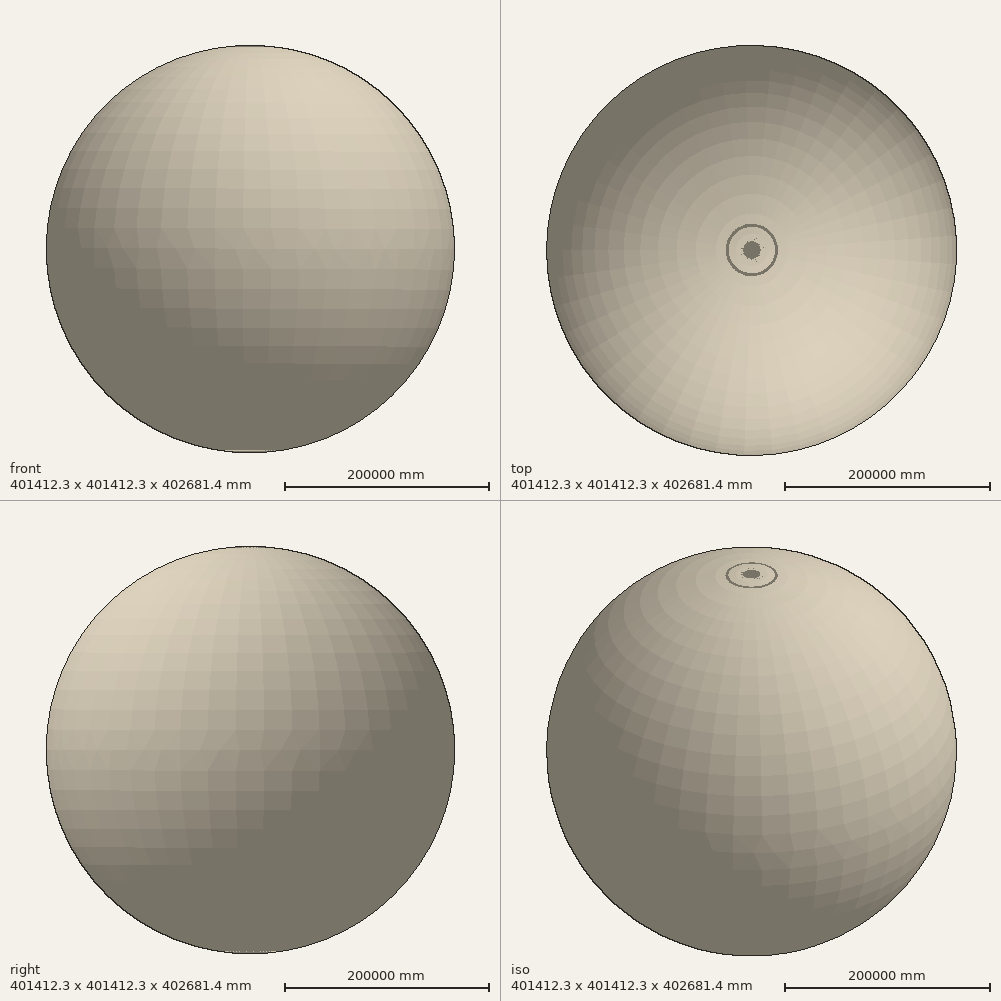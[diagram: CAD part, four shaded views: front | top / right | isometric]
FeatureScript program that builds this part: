
annotation { "Feature Type Name" : "Feature", "Feature Type Description" : "" }
export const myFeature = defineFeature(function(context is Context, id is Id, definition is map)
    precondition{}
    {
        {
            var Q0;
            Q0=qCreatedBy(makeId("Front.planeOp"),FACE);
            var sketch = newSketch(context, id + "F0", { "sketchPlane" : qUnion([Q0])});
            skLineSegment(sketch, "E0", {"start": v(0, 26.35) * mm, "end": v(23.53, 26.35) * mm});
            skLineSegment(sketch, "E1", {"start": v(23.53, 26.35) * mm, "end": v(0, -71.85) * mm});
            skLineSegment(sketch, "E2", {"start": v(0, 0) * mm, "end": v(0, 26.35) * mm});
            skLineSegment(sketch, "E3", {"start": v(0, 26.35) * mm, "end": v(0, -71.85) * mm});
            skSolve(sketch);
        }
        {
            var Q0;
            Q0 = qSketchRegion(id + "F0", true);
            var Q1;
            Q1=sQuery(id+"F0.wireOp",EDGE,"E3");
            revolve(context, id + "F1", {"entities" : qUnion([Q0]), "axis" : qUnion([Q1]), "revolveType" : RevolveType.FULL});
        }
        {
            var Q0;
            Q0=qCreatedBy(makeId("Front.planeOp"),FACE);
            var sketch = newSketch(context, id + "F2", { "sketchPlane" : qUnion([Q0])});
            skArc(sketch, "E4", {"start": v(-1412.3, 2609.59) * mm, "mid": v(199998.75, 201898.44) * mm, "end": v(0, 402604.6) * mm});
            skLineSegment(sketch, "E5", {"start": v(-1412.3, 2609.59) * mm, "end": v(0, 402604.6) * mm});
            skSolve(sketch);
        }
        {
            var Q0;
            Q0 = qSketchRegion(id + "F2", true);
            var Q1;
            Q1=sQuery(id+"F2.wireOp",EDGE,"E5");
            revolve(context, id + "F3", {"entities" : qUnion([Q0]), "axis" : qUnion([Q1]), "revolveType" : RevolveType.FULL});
        }
    });
